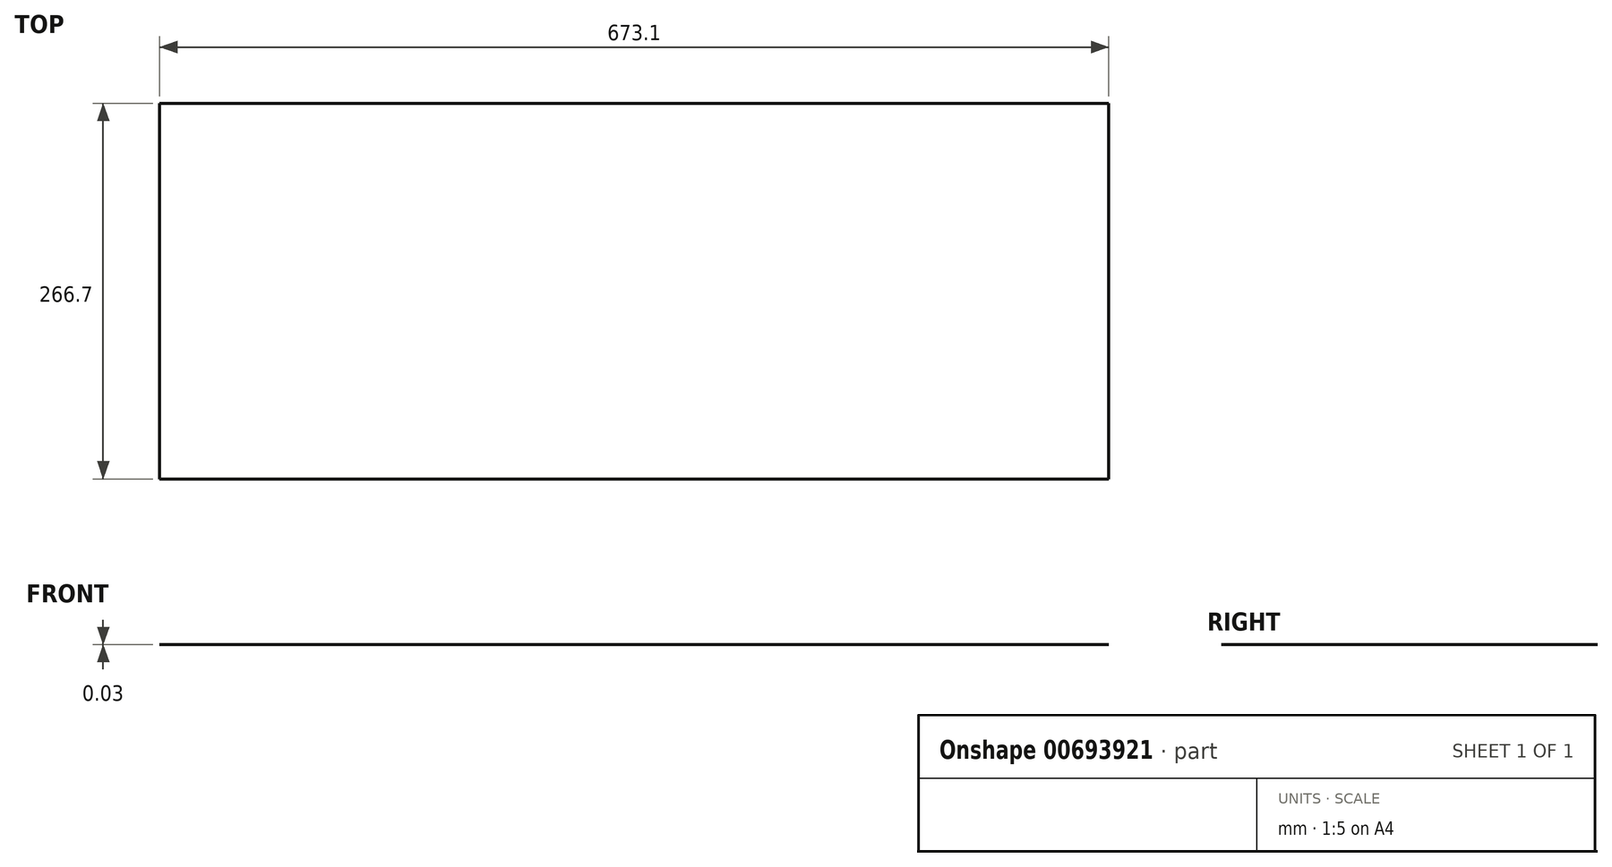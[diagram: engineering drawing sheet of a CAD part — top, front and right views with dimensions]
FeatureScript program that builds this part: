
annotation { "Feature Type Name" : "Feature", "Feature Type Description" : "" }
export const myFeature = defineFeature(function(context is Context, id is Id, definition is map)
    precondition{}
    {
        {
            var Q0;
            Q0=qCreatedBy(makeId("Top.planeOp"),FACE);
            var sketch = newSketch(context, id + "F0", { "sketchPlane" : qUnion([Q0])});
            skLineSegment(sketch, "E0.bottom", {"start": v(-336.55, 133.35) * mm, "end": v(336.55, 133.35) * mm});
            skLineSegment(sketch, "E0.top", {"start": v(-336.55, -133.35) * mm, "end": v(336.55, -133.35) * mm});
            skLineSegment(sketch, "E0.left", {"start": v(-336.55, 133.35) * mm, "end": v(-336.55, -133.35) * mm});
            skLineSegment(sketch, "E0.right", {"start": v(336.55, 133.35) * mm, "end": v(336.55, -133.35) * mm});
            skPoint(sketch, "E0.middle", {"position": v(0, 0) * mm});
            skSolve(sketch);
        }
        {
            var Q0;
            Q0=makeQuery(id+"F0.imprint","IMPRINT",FACE,{"disambiguationData":[TD([[makeQuery(id+"F0.imprint","IMPRINT",EDGE,{"derivedFrom":sQuery(id+"F0.wireOp",EDGE,"E0.bottom")}),-1.0]])]});
            extrude(context, id + "F1", {"entities" : qUnion([Q0]), "depth" : 3 / 101.6 * mm});
        }
    });
